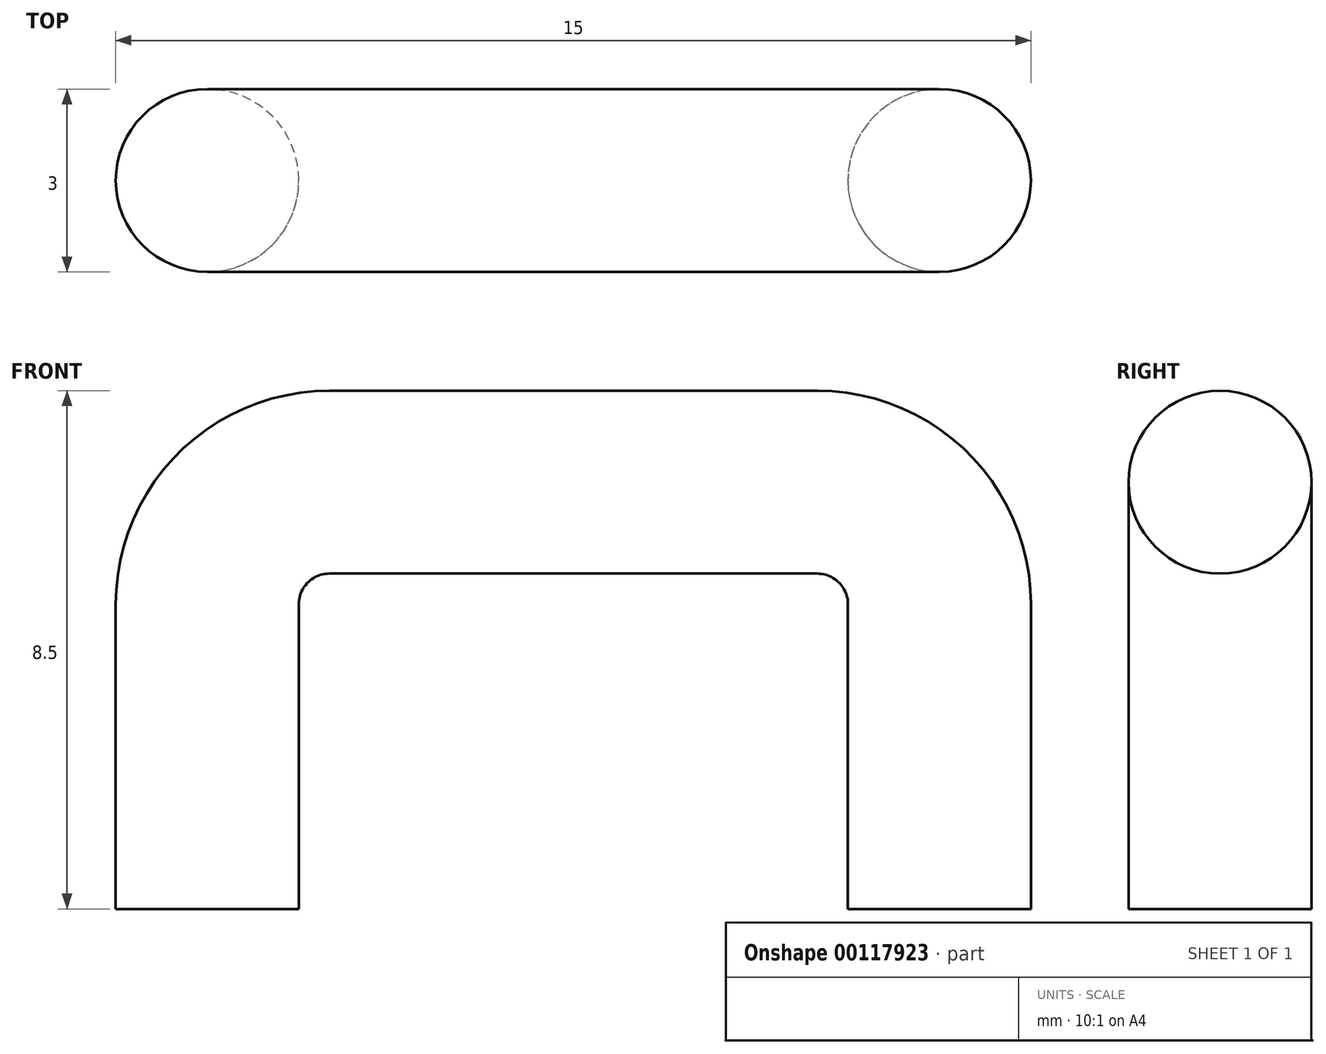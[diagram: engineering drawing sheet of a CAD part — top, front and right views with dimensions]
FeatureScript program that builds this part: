
annotation { "Feature Type Name" : "Feature", "Feature Type Description" : "" }
export const myFeature = defineFeature(function(context is Context, id is Id, definition is map)
    precondition{}
    {
        {
            var Q0;
            Q0=qCreatedBy(makeId("Top.planeOp"),FACE);
            var sketch = newSketch(context, id + "F0", { "sketchPlane" : qUnion([Q0])});
            skCircle(sketch, "E0", {"center": v(-6, 0) * mm, "radius": 1.5 * mm});
            skSolve(sketch);
        }
        {
            var Q0;
            Q0=qCreatedBy(makeId("Front.planeOp"),FACE);
            var sketch = newSketch(context, id + "F1", { "sketchPlane" : qUnion([Q0])});
            skLineSegment(sketch, "E1", {"start": v(-6, 0) * mm, "end": v(-6, 5) * mm});
            skLineSegment(sketch, "E2", {"start": v(-4, 7) * mm, "end": v(0, 7) * mm});
            skPoint(sketch, "E3.visualSharp", {"position": v(-6, 7) * mm});
            skArc(sketch, "E3.filletArc", {"start": v(-4, 7) * mm, "mid": v(-5.41, 6.41) * mm, "end": v(-6, 5) * mm});
            skSolve(sketch);
        }
        {
            var Q0;
            Q0 = qSketchRegion(id + "F0", true);
            var Q1;
            Q1 = qConstructionFilter(qBodyType(qCreatedBy(id + "F1" ,EDGE), BodyType.WIRE), ConstructionObject.NO);
            sweep(context, id + "F2", {"profiles" : qUnion([Q0]), "path" : qUnion([Q1])});
        }
        {
            var Q0;
            Q0=makeQuery(id+"F2.opSweep","SWEPT_BODY",BODY,{"disambiguationData":[OSD([sQuery(id+"F0.wireOp",EDGE,"E0"),sQuery(id+"F1.wireOp",EDGE,"E1")])]});
            var Q1;
            Q1=qCreatedBy(makeId("Right.planeOp"),FACE);
            mirror(context, id + "F3", {"operationType" : NewBodyOperationType.ADD, "entities" : qUnion([Q0]), "mirrorPlane" : qUnion([Q1])});
        }
    });
